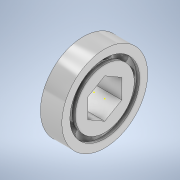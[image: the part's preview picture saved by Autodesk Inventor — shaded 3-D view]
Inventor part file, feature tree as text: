
AUTODESK INVENTOR PART (.ipt)
format: ipt  version: 2020.3 (Build 243373000, 373)  size: 284,160 bytes
history: native  units: mm
features: sketch x11, extrude x3, revolve x2, pattern_circular x1, projected_geometry x1
ambient origin geometry x8: Origin, YZ Plane, XZ Plane, XY Plane, X Axis, Y Axis, Z Axis, Center Point
bodies: Solid1 (feature_tree)
feature tree (18):
  sketch  "Sketch1"  dims[d6=8.0mm d7=3.0mm]
  sketch  "Sketch2"  dims[d8=8.0mm d9=3.0mm]
  revolve  "Revolution1"  [1 undecoded]
  sketch  "Sketch5"  dims[d10=2.0mm d11=8.0mm]
  sketch  "Sketch6"  dims[d12=6.0mm d13=1.0mm]
  sketch  "Sketch7"  dims[d15=90.0deg]
  revolve  "Revolution2"  [1 undecoded]
  pattern_circular  "Circular Pattern1"  Count=10 Angle=360.0deg
  sketch  "Sketch9"  dims[d17=90.0deg d18=100.0mm d19=360.0deg]
  sketch  "Sketch10"  dims[d21=8.0mm d22=0.0mm d23=15.75mm]
  extrude  "Extrusion1"  Depth=8.0mm
  extrude  "Extrusion2"  Depth=3.0mm TaperAngle=0.0deg
  extrude  "Extrusion3"  Depth=11.0mm TaperAngle=0.0deg
  sketch  "Sketch8"  dims[d16=4.6mm]
  projected_geometry  "Projected Loop1"
  sketch  "Sketch11"  dims[d24=12.7mm d25=3.0mm d26=0.0mm]
  sketch  "Sketch12"  dims[d27=12.7mm d28=11.0mm d29=0.0mm]
  sketch  "Sketch13"
note: 2 required parameter values undecoded (feature->parameter linkage not recoverable at this tier; creation-order binding heuristic only, values carry confidence <= 0.55)
